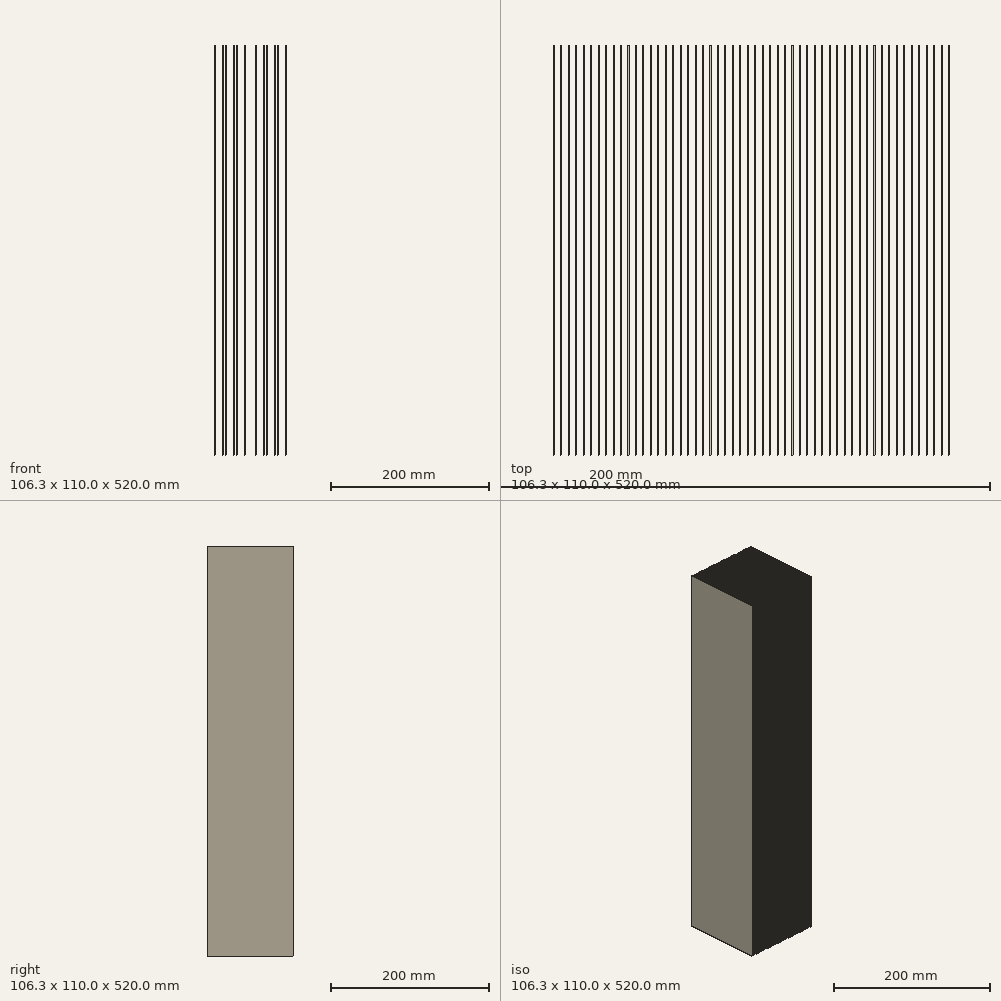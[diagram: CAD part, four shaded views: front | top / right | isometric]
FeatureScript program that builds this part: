
annotation { "Feature Type Name" : "Feature", "Feature Type Description" : "" }
export const myFeature = defineFeature(function(context is Context, id is Id, definition is map)
    precondition{}
    {
        {
            var Q0;
            Q0=qCreatedBy(makeId("Top.planeOp"),FACE);
            var sketch = newSketch(context, id + "F0", { "sketchPlane" : qUnion([Q0])});
            skLineSegment(sketch, "E0.bottom", {"start": v(-88.02, 70.44) * mm, "end": v(21.98, 70.44) * mm});
            skLineSegment(sketch, "E0.top", {"start": v(-88.02, -39.56) * mm, "end": v(21.98, -39.56) * mm});
            skLineSegment(sketch, "E0.left", {"start": v(-88.02, 70.44) * mm, "end": v(-88.02, -39.56) * mm});
            skLineSegment(sketch, "E0.right", {"start": v(21.98, 70.44) * mm, "end": v(21.98, -39.56) * mm});
            skSolve(sketch);
        }
        {
            var Q0;
            Q0 = qSketchRegion(id + "F0", true);
            extrude(context, id + "F1", {"entities" : qUnion([Q0]), "depth" : 520 * mm});
        }
        {
            var Q0;
            Q0=makeQuery(id+"F1.opExtrude","SWEPT_FACE",FACE,{"disambiguationData":[OSD([sQuery(id+"F0.wireOp",EDGE,"E0.top")])]});
            var sketch = newSketch(context, id + "F2", { "sketchPlane" : qUnion([Q0])});
            skLineSegment(sketch, "E1.bottom", {"start": v(-86.02, 520) * mm, "end": v(-85.72, 520) * mm});
            skLineSegment(sketch, "E1.top", {"start": v(-86.02, 0) * mm, "end": v(-85.72, 0) * mm});
            skLineSegment(sketch, "E1.left", {"start": v(-86.02, 520) * mm, "end": v(-86.02, 0) * mm});
            skLineSegment(sketch, "E1.right", {"start": v(-85.72, 520) * mm, "end": v(-85.72, 0) * mm});
            skLineSegment(sketch, "E2.1.0.0", {"start": v(-83.72, 520) * mm, "end": v(-83.72, 0) * mm});
            skLineSegment(sketch, "E2.1.0.1", {"start": v(-84.02, 520) * mm, "end": v(-84.02, 0) * mm});
            skLineSegment(sketch, "E2.1.0.2", {"start": v(-84.02, 0) * mm, "end": v(-83.72, 0) * mm});
            skLineSegment(sketch, "E2.1.0.3", {"start": v(-84.02, 520) * mm, "end": v(-83.72, 520) * mm});
            skLineSegment(sketch, "E2.2.0.0", {"start": v(-81.72, 520) * mm, "end": v(-81.72, 0) * mm});
            skLineSegment(sketch, "E2.2.0.1", {"start": v(-82.02, 520) * mm, "end": v(-82.02, 0) * mm});
            skLineSegment(sketch, "E2.2.0.2", {"start": v(-82.02, 0) * mm, "end": v(-81.72, 0) * mm});
            skLineSegment(sketch, "E2.2.0.3", {"start": v(-82.02, 520) * mm, "end": v(-81.72, 520) * mm});
            skLineSegment(sketch, "E2.3.0.0", {"start": v(-79.72, 520) * mm, "end": v(-79.72, 0) * mm});
            skLineSegment(sketch, "E2.3.0.1", {"start": v(-80.02, 520) * mm, "end": v(-80.02, 0) * mm});
            skLineSegment(sketch, "E2.3.0.2", {"start": v(-80.02, 0) * mm, "end": v(-79.72, 0) * mm});
            skLineSegment(sketch, "E2.3.0.3", {"start": v(-80.02, 520) * mm, "end": v(-79.72, 520) * mm});
            skLineSegment(sketch, "E2.4.0.0", {"start": v(-77.72, 520) * mm, "end": v(-77.72, 0) * mm});
            skLineSegment(sketch, "E2.4.0.1", {"start": v(-78.02, 520) * mm, "end": v(-78.02, 0) * mm});
            skLineSegment(sketch, "E2.4.0.2", {"start": v(-78.02, 0) * mm, "end": v(-77.72, 0) * mm});
            skLineSegment(sketch, "E2.4.0.3", {"start": v(-78.02, 520) * mm, "end": v(-77.72, 520) * mm});
            skLineSegment(sketch, "E2.5.0.0", {"start": v(-75.72, 520) * mm, "end": v(-75.72, 0) * mm});
            skLineSegment(sketch, "E2.5.0.1", {"start": v(-76.02, 520) * mm, "end": v(-76.02, 0) * mm});
            skLineSegment(sketch, "E2.5.0.2", {"start": v(-76.02, 0) * mm, "end": v(-75.72, 0) * mm});
            skLineSegment(sketch, "E2.5.0.3", {"start": v(-76.02, 520) * mm, "end": v(-75.72, 520) * mm});
            skLineSegment(sketch, "E2.6.0.0", {"start": v(-73.72, 520) * mm, "end": v(-73.72, 0) * mm});
            skLineSegment(sketch, "E2.6.0.1", {"start": v(-74.02, 520) * mm, "end": v(-74.02, 0) * mm});
            skLineSegment(sketch, "E2.6.0.2", {"start": v(-74.02, 0) * mm, "end": v(-73.72, 0) * mm});
            skLineSegment(sketch, "E2.6.0.3", {"start": v(-74.02, 520) * mm, "end": v(-73.72, 520) * mm});
            skLineSegment(sketch, "E2.7.0.0", {"start": v(-71.72, 520) * mm, "end": v(-71.72, 0) * mm});
            skLineSegment(sketch, "E2.7.0.1", {"start": v(-72.02, 520) * mm, "end": v(-72.02, 0) * mm});
            skLineSegment(sketch, "E2.7.0.2", {"start": v(-72.02, 0) * mm, "end": v(-71.72, 0) * mm});
            skLineSegment(sketch, "E2.7.0.3", {"start": v(-72.02, 520) * mm, "end": v(-71.72, 520) * mm});
            skLineSegment(sketch, "E2.8.0.0", {"start": v(-69.72, 520) * mm, "end": v(-69.72, 0) * mm});
            skLineSegment(sketch, "E2.8.0.1", {"start": v(-70.02, 520) * mm, "end": v(-70.02, 0) * mm});
            skLineSegment(sketch, "E2.8.0.2", {"start": v(-70.02, 0) * mm, "end": v(-69.72, 0) * mm});
            skLineSegment(sketch, "E2.8.0.3", {"start": v(-70.02, 520) * mm, "end": v(-69.72, 520) * mm});
            skLineSegment(sketch, "E2.9.0.0", {"start": v(-67.72, 520) * mm, "end": v(-67.72, 0) * mm});
            skLineSegment(sketch, "E2.9.0.1", {"start": v(-68.02, 520) * mm, "end": v(-68.02, 0) * mm});
            skLineSegment(sketch, "E2.9.0.2", {"start": v(-68.02, 0) * mm, "end": v(-67.72, 0) * mm});
            skLineSegment(sketch, "E2.9.0.3", {"start": v(-68.02, 520) * mm, "end": v(-67.72, 520) * mm});
            skLineSegment(sketch, "E2.10.0.0", {"start": v(-65.72, 520) * mm, "end": v(-65.72, 0) * mm});
            skLineSegment(sketch, "E2.10.0.1", {"start": v(-66.02, 520) * mm, "end": v(-66.02, 0) * mm});
            skLineSegment(sketch, "E2.10.0.2", {"start": v(-66.02, 0) * mm, "end": v(-65.72, 0) * mm});
            skLineSegment(sketch, "E2.10.0.3", {"start": v(-66.02, 520) * mm, "end": v(-65.72, 520) * mm});
            skLineSegment(sketch, "E2.11.0.0", {"start": v(-63.72, 520) * mm, "end": v(-63.72, 0) * mm});
            skLineSegment(sketch, "E2.11.0.1", {"start": v(-64.02, 520) * mm, "end": v(-64.02, 0) * mm});
            skLineSegment(sketch, "E2.11.0.2", {"start": v(-64.02, 0) * mm, "end": v(-63.72, 0) * mm});
            skLineSegment(sketch, "E2.11.0.3", {"start": v(-64.02, 520) * mm, "end": v(-63.72, 520) * mm});
            skLineSegment(sketch, "E2.12.0.0", {"start": v(-61.72, 520) * mm, "end": v(-61.72, 0) * mm});
            skLineSegment(sketch, "E2.12.0.1", {"start": v(-62.02, 520) * mm, "end": v(-62.02, 0) * mm});
            skLineSegment(sketch, "E2.12.0.2", {"start": v(-62.02, 0) * mm, "end": v(-61.72, 0) * mm});
            skLineSegment(sketch, "E2.12.0.3", {"start": v(-62.02, 520) * mm, "end": v(-61.72, 520) * mm});
            skLineSegment(sketch, "E2.13.0.0", {"start": v(-59.72, 520) * mm, "end": v(-59.72, 0) * mm});
            skLineSegment(sketch, "E2.13.0.1", {"start": v(-60.02, 520) * mm, "end": v(-60.02, 0) * mm});
            skLineSegment(sketch, "E2.13.0.2", {"start": v(-60.02, 0) * mm, "end": v(-59.72, 0) * mm});
            skLineSegment(sketch, "E2.13.0.3", {"start": v(-60.02, 520) * mm, "end": v(-59.72, 520) * mm});
            skLineSegment(sketch, "E2.14.0.0", {"start": v(-57.72, 520) * mm, "end": v(-57.72, 0) * mm});
            skLineSegment(sketch, "E2.14.0.1", {"start": v(-58.02, 520) * mm, "end": v(-58.02, 0) * mm});
            skLineSegment(sketch, "E2.14.0.2", {"start": v(-58.02, 0) * mm, "end": v(-57.72, 0) * mm});
            skLineSegment(sketch, "E2.14.0.3", {"start": v(-58.02, 520) * mm, "end": v(-57.72, 520) * mm});
            skLineSegment(sketch, "E2.15.0.0", {"start": v(-55.72, 520) * mm, "end": v(-55.72, 0) * mm});
            skLineSegment(sketch, "E2.15.0.1", {"start": v(-56.02, 520) * mm, "end": v(-56.02, 0) * mm});
            skLineSegment(sketch, "E2.15.0.2", {"start": v(-56.02, 0) * mm, "end": v(-55.72, 0) * mm});
            skLineSegment(sketch, "E2.15.0.3", {"start": v(-56.02, 520) * mm, "end": v(-55.72, 520) * mm});
            skLineSegment(sketch, "E2.16.0.0", {"start": v(-53.72, 520) * mm, "end": v(-53.72, 0) * mm});
            skLineSegment(sketch, "E2.16.0.1", {"start": v(-54.02, 520) * mm, "end": v(-54.02, 0) * mm});
            skLineSegment(sketch, "E2.16.0.2", {"start": v(-54.02, 0) * mm, "end": v(-53.72, 0) * mm});
            skLineSegment(sketch, "E2.16.0.3", {"start": v(-54.02, 520) * mm, "end": v(-53.72, 520) * mm});
            skLineSegment(sketch, "E2.17.0.0", {"start": v(-51.72, 520) * mm, "end": v(-51.72, 0) * mm});
            skLineSegment(sketch, "E2.17.0.1", {"start": v(-52.02, 520) * mm, "end": v(-52.02, 0) * mm});
            skLineSegment(sketch, "E2.17.0.2", {"start": v(-52.02, 0) * mm, "end": v(-51.72, 0) * mm});
            skLineSegment(sketch, "E2.17.0.3", {"start": v(-52.02, 520) * mm, "end": v(-51.72, 520) * mm});
            skLineSegment(sketch, "E2.18.0.0", {"start": v(-49.72, 520) * mm, "end": v(-49.72, 0) * mm});
            skLineSegment(sketch, "E2.18.0.1", {"start": v(-50.02, 520) * mm, "end": v(-50.02, 0) * mm});
            skLineSegment(sketch, "E2.18.0.2", {"start": v(-50.02, 0) * mm, "end": v(-49.72, 0) * mm});
            skLineSegment(sketch, "E2.18.0.3", {"start": v(-50.02, 520) * mm, "end": v(-49.72, 520) * mm});
            skLineSegment(sketch, "E2.19.0.0", {"start": v(-47.72, 520) * mm, "end": v(-47.72, 0) * mm});
            skLineSegment(sketch, "E2.19.0.1", {"start": v(-48.02, 520) * mm, "end": v(-48.02, 0) * mm});
            skLineSegment(sketch, "E2.19.0.2", {"start": v(-48.02, 0) * mm, "end": v(-47.72, 0) * mm});
            skLineSegment(sketch, "E2.19.0.3", {"start": v(-48.02, 520) * mm, "end": v(-47.72, 520) * mm});
            skLineSegment(sketch, "E2.20.0.0", {"start": v(-45.72, 520) * mm, "end": v(-45.72, 0) * mm});
            skLineSegment(sketch, "E2.20.0.1", {"start": v(-46.02, 520) * mm, "end": v(-46.02, 0) * mm});
            skLineSegment(sketch, "E2.20.0.2", {"start": v(-46.02, 0) * mm, "end": v(-45.72, 0) * mm});
            skLineSegment(sketch, "E2.20.0.3", {"start": v(-46.02, 520) * mm, "end": v(-45.72, 520) * mm});
            skLineSegment(sketch, "E2.21.0.0", {"start": v(-43.72, 520) * mm, "end": v(-43.72, 0) * mm});
            skLineSegment(sketch, "E2.21.0.1", {"start": v(-44.02, 520) * mm, "end": v(-44.02, 0) * mm});
            skLineSegment(sketch, "E2.21.0.2", {"start": v(-44.02, 0) * mm, "end": v(-43.72, 0) * mm});
            skLineSegment(sketch, "E2.21.0.3", {"start": v(-44.02, 520) * mm, "end": v(-43.72, 520) * mm});
            skLineSegment(sketch, "E2.22.0.0", {"start": v(-41.72, 520) * mm, "end": v(-41.72, 0) * mm});
            skLineSegment(sketch, "E2.22.0.1", {"start": v(-42.02, 520) * mm, "end": v(-42.02, 0) * mm});
            skLineSegment(sketch, "E2.22.0.2", {"start": v(-42.02, 0) * mm, "end": v(-41.72, 0) * mm});
            skLineSegment(sketch, "E2.22.0.3", {"start": v(-42.02, 520) * mm, "end": v(-41.72, 520) * mm});
            skLineSegment(sketch, "E2.23.0.0", {"start": v(-39.72, 520) * mm, "end": v(-39.72, 0) * mm});
            skLineSegment(sketch, "E2.23.0.1", {"start": v(-40.02, 520) * mm, "end": v(-40.02, 0) * mm});
            skLineSegment(sketch, "E2.23.0.2", {"start": v(-40.02, 0) * mm, "end": v(-39.72, 0) * mm});
            skLineSegment(sketch, "E2.23.0.3", {"start": v(-40.02, 520) * mm, "end": v(-39.72, 520) * mm});
            skLineSegment(sketch, "E2.24.0.0", {"start": v(-37.72, 520) * mm, "end": v(-37.72, 0) * mm});
            skLineSegment(sketch, "E2.24.0.1", {"start": v(-38.02, 520) * mm, "end": v(-38.02, 0) * mm});
            skLineSegment(sketch, "E2.24.0.2", {"start": v(-38.02, 0) * mm, "end": v(-37.72, 0) * mm});
            skLineSegment(sketch, "E2.24.0.3", {"start": v(-38.02, 520) * mm, "end": v(-37.72, 520) * mm});
            skLineSegment(sketch, "E2.25.0.0", {"start": v(-35.72, 520) * mm, "end": v(-35.72, 0) * mm});
            skLineSegment(sketch, "E2.25.0.1", {"start": v(-36.02, 520) * mm, "end": v(-36.02, 0) * mm});
            skLineSegment(sketch, "E2.25.0.2", {"start": v(-36.02, 0) * mm, "end": v(-35.72, 0) * mm});
            skLineSegment(sketch, "E2.25.0.3", {"start": v(-36.02, 520) * mm, "end": v(-35.72, 520) * mm});
            skLineSegment(sketch, "E2.26.0.0", {"start": v(-33.72, 520) * mm, "end": v(-33.72, 0) * mm});
            skLineSegment(sketch, "E2.26.0.1", {"start": v(-34.02, 520) * mm, "end": v(-34.02, 0) * mm});
            skLineSegment(sketch, "E2.26.0.2", {"start": v(-34.02, 0) * mm, "end": v(-33.72, 0) * mm});
            skLineSegment(sketch, "E2.26.0.3", {"start": v(-34.02, 520) * mm, "end": v(-33.72, 520) * mm});
            skLineSegment(sketch, "E2.27.0.0", {"start": v(-31.72, 520) * mm, "end": v(-31.72, 0) * mm});
            skLineSegment(sketch, "E2.27.0.1", {"start": v(-32.02, 520) * mm, "end": v(-32.02, 0) * mm});
            skLineSegment(sketch, "E2.27.0.2", {"start": v(-32.02, 0) * mm, "end": v(-31.72, 0) * mm});
            skLineSegment(sketch, "E2.27.0.3", {"start": v(-32.02, 520) * mm, "end": v(-31.72, 520) * mm});
            skLineSegment(sketch, "E2.28.0.0", {"start": v(-29.72, 520) * mm, "end": v(-29.72, 0) * mm});
            skLineSegment(sketch, "E2.28.0.1", {"start": v(-30.02, 520) * mm, "end": v(-30.02, 0) * mm});
            skLineSegment(sketch, "E2.28.0.2", {"start": v(-30.02, 0) * mm, "end": v(-29.72, 0) * mm});
            skLineSegment(sketch, "E2.28.0.3", {"start": v(-30.02, 520) * mm, "end": v(-29.72, 520) * mm});
            skLineSegment(sketch, "E2.29.0.0", {"start": v(-27.72, 520) * mm, "end": v(-27.72, 0) * mm});
            skLineSegment(sketch, "E2.29.0.1", {"start": v(-28.02, 520) * mm, "end": v(-28.02, 0) * mm});
            skLineSegment(sketch, "E2.29.0.2", {"start": v(-28.02, 0) * mm, "end": v(-27.72, 0) * mm});
            skLineSegment(sketch, "E2.29.0.3", {"start": v(-28.02, 520) * mm, "end": v(-27.72, 520) * mm});
            skLineSegment(sketch, "E2.30.0.0", {"start": v(-25.72, 520) * mm, "end": v(-25.72, 0) * mm});
            skLineSegment(sketch, "E2.30.0.1", {"start": v(-26.02, 520) * mm, "end": v(-26.02, 0) * mm});
            skLineSegment(sketch, "E2.30.0.2", {"start": v(-26.02, 0) * mm, "end": v(-25.72, 0) * mm});
            skLineSegment(sketch, "E2.30.0.3", {"start": v(-26.02, 520) * mm, "end": v(-25.72, 520) * mm});
            skLineSegment(sketch, "E2.31.0.0", {"start": v(-23.72, 520) * mm, "end": v(-23.72, 0) * mm});
            skLineSegment(sketch, "E2.31.0.1", {"start": v(-24.02, 520) * mm, "end": v(-24.02, 0) * mm});
            skLineSegment(sketch, "E2.31.0.2", {"start": v(-24.02, 0) * mm, "end": v(-23.72, 0) * mm});
            skLineSegment(sketch, "E2.31.0.3", {"start": v(-24.02, 520) * mm, "end": v(-23.72, 520) * mm});
            skLineSegment(sketch, "E2.32.0.0", {"start": v(-21.72, 520) * mm, "end": v(-21.72, 0) * mm});
            skLineSegment(sketch, "E2.32.0.1", {"start": v(-22.02, 520) * mm, "end": v(-22.02, 0) * mm});
            skLineSegment(sketch, "E2.32.0.2", {"start": v(-22.02, 0) * mm, "end": v(-21.72, 0) * mm});
            skLineSegment(sketch, "E2.32.0.3", {"start": v(-22.02, 520) * mm, "end": v(-21.72, 520) * mm});
            skLineSegment(sketch, "E2.33.0.0", {"start": v(-19.72, 520) * mm, "end": v(-19.72, 0) * mm});
            skLineSegment(sketch, "E2.33.0.1", {"start": v(-20.02, 520) * mm, "end": v(-20.02, 0) * mm});
            skLineSegment(sketch, "E2.33.0.2", {"start": v(-20.02, 0) * mm, "end": v(-19.72, 0) * mm});
            skLineSegment(sketch, "E2.33.0.3", {"start": v(-20.02, 520) * mm, "end": v(-19.72, 520) * mm});
            skLineSegment(sketch, "E2.34.0.0", {"start": v(-17.72, 520) * mm, "end": v(-17.72, 0) * mm});
            skLineSegment(sketch, "E2.34.0.1", {"start": v(-18.02, 520) * mm, "end": v(-18.02, 0) * mm});
            skLineSegment(sketch, "E2.34.0.2", {"start": v(-18.02, 0) * mm, "end": v(-17.72, 0) * mm});
            skLineSegment(sketch, "E2.34.0.3", {"start": v(-18.02, 520) * mm, "end": v(-17.72, 520) * mm});
            skLineSegment(sketch, "E2.35.0.0", {"start": v(-15.72, 520) * mm, "end": v(-15.72, 0) * mm});
            skLineSegment(sketch, "E2.35.0.1", {"start": v(-16.02, 520) * mm, "end": v(-16.02, 0) * mm});
            skLineSegment(sketch, "E2.35.0.2", {"start": v(-16.02, 0) * mm, "end": v(-15.72, 0) * mm});
            skLineSegment(sketch, "E2.35.0.3", {"start": v(-16.02, 520) * mm, "end": v(-15.72, 520) * mm});
            skLineSegment(sketch, "E2.36.0.0", {"start": v(-13.72, 520) * mm, "end": v(-13.72, 0) * mm});
            skLineSegment(sketch, "E2.36.0.1", {"start": v(-14.02, 520) * mm, "end": v(-14.02, 0) * mm});
            skLineSegment(sketch, "E2.36.0.2", {"start": v(-14.02, 0) * mm, "end": v(-13.72, 0) * mm});
            skLineSegment(sketch, "E2.36.0.3", {"start": v(-14.02, 520) * mm, "end": v(-13.72, 520) * mm});
            skLineSegment(sketch, "E2.37.0.0", {"start": v(-11.72, 520) * mm, "end": v(-11.72, 0) * mm});
            skLineSegment(sketch, "E2.37.0.1", {"start": v(-12.02, 520) * mm, "end": v(-12.02, 0) * mm});
            skLineSegment(sketch, "E2.37.0.2", {"start": v(-12.02, 0) * mm, "end": v(-11.72, 0) * mm});
            skLineSegment(sketch, "E2.37.0.3", {"start": v(-12.02, 520) * mm, "end": v(-11.72, 520) * mm});
            skLineSegment(sketch, "E2.38.0.0", {"start": v(-9.72, 520) * mm, "end": v(-9.72, 0) * mm});
            skLineSegment(sketch, "E2.38.0.1", {"start": v(-10.02, 520) * mm, "end": v(-10.02, 0) * mm});
            skLineSegment(sketch, "E2.38.0.2", {"start": v(-10.02, 0) * mm, "end": v(-9.72, 0) * mm});
            skLineSegment(sketch, "E2.38.0.3", {"start": v(-10.02, 520) * mm, "end": v(-9.72, 520) * mm});
            skLineSegment(sketch, "E2.39.0.0", {"start": v(-7.72, 520) * mm, "end": v(-7.72, 0) * mm});
            skLineSegment(sketch, "E2.39.0.1", {"start": v(-8.02, 520) * mm, "end": v(-8.02, 0) * mm});
            skLineSegment(sketch, "E2.39.0.2", {"start": v(-8.02, 0) * mm, "end": v(-7.72, 0) * mm});
            skLineSegment(sketch, "E2.39.0.3", {"start": v(-8.02, 520) * mm, "end": v(-7.72, 520) * mm});
            skLineSegment(sketch, "E2.40.0.0", {"start": v(-5.72, 520) * mm, "end": v(-5.72, 0) * mm});
            skLineSegment(sketch, "E2.40.0.1", {"start": v(-6.02, 520) * mm, "end": v(-6.02, 0) * mm});
            skLineSegment(sketch, "E2.40.0.2", {"start": v(-6.02, 0) * mm, "end": v(-5.72, 0) * mm});
            skLineSegment(sketch, "E2.40.0.3", {"start": v(-6.02, 520) * mm, "end": v(-5.72, 520) * mm});
            skLineSegment(sketch, "E2.41.0.0", {"start": v(-3.72, 520) * mm, "end": v(-3.72, 0) * mm});
            skLineSegment(sketch, "E2.41.0.1", {"start": v(-4.02, 520) * mm, "end": v(-4.02, 0) * mm});
            skLineSegment(sketch, "E2.41.0.2", {"start": v(-4.02, 0) * mm, "end": v(-3.72, 0) * mm});
            skLineSegment(sketch, "E2.41.0.3", {"start": v(-4.02, 520) * mm, "end": v(-3.72, 520) * mm});
            skLineSegment(sketch, "E2.42.0.0", {"start": v(-1.72, 520) * mm, "end": v(-1.72, 0) * mm});
            skLineSegment(sketch, "E2.42.0.1", {"start": v(-2.02, 520) * mm, "end": v(-2.02, 0) * mm});
            skLineSegment(sketch, "E2.42.0.2", {"start": v(-2.02, 0) * mm, "end": v(-1.72, 0) * mm});
            skLineSegment(sketch, "E2.42.0.3", {"start": v(-2.02, 520) * mm, "end": v(-1.72, 520) * mm});
            skLineSegment(sketch, "E2.43.0.0", {"start": v(0.28, 520) * mm, "end": v(0.28, 0) * mm});
            skLineSegment(sketch, "E2.43.0.1", {"start": v(-0.02, 520) * mm, "end": v(-0.02, 0) * mm});
            skLineSegment(sketch, "E2.43.0.2", {"start": v(-0.02, 0) * mm, "end": v(0.28, 0) * mm});
            skLineSegment(sketch, "E2.43.0.3", {"start": v(-0.02, 520) * mm, "end": v(0.28, 520) * mm});
            skLineSegment(sketch, "E2.44.0.0", {"start": v(2.28, 520) * mm, "end": v(2.28, 0) * mm});
            skLineSegment(sketch, "E2.44.0.1", {"start": v(1.98, 520) * mm, "end": v(1.98, 0) * mm});
            skLineSegment(sketch, "E2.44.0.2", {"start": v(1.98, 0) * mm, "end": v(2.28, 0) * mm});
            skLineSegment(sketch, "E2.44.0.3", {"start": v(1.98, 520) * mm, "end": v(2.28, 520) * mm});
            skLineSegment(sketch, "E2.45.0.0", {"start": v(4.28, 520) * mm, "end": v(4.28, 0) * mm});
            skLineSegment(sketch, "E2.45.0.1", {"start": v(3.98, 520) * mm, "end": v(3.98, 0) * mm});
            skLineSegment(sketch, "E2.45.0.2", {"start": v(3.98, 0) * mm, "end": v(4.28, 0) * mm});
            skLineSegment(sketch, "E2.45.0.3", {"start": v(3.98, 520) * mm, "end": v(4.28, 520) * mm});
            skLineSegment(sketch, "E2.46.0.0", {"start": v(6.28, 520) * mm, "end": v(6.28, 0) * mm});
            skLineSegment(sketch, "E2.46.0.1", {"start": v(5.98, 520) * mm, "end": v(5.98, 0) * mm});
            skLineSegment(sketch, "E2.46.0.2", {"start": v(5.98, 0) * mm, "end": v(6.28, 0) * mm});
            skLineSegment(sketch, "E2.46.0.3", {"start": v(5.98, 520) * mm, "end": v(6.28, 520) * mm});
            skLineSegment(sketch, "E2.47.0.0", {"start": v(8.28, 520) * mm, "end": v(8.28, 0) * mm});
            skLineSegment(sketch, "E2.47.0.1", {"start": v(7.98, 520) * mm, "end": v(7.98, 0) * mm});
            skLineSegment(sketch, "E2.47.0.2", {"start": v(7.98, 0) * mm, "end": v(8.28, 0) * mm});
            skLineSegment(sketch, "E2.47.0.3", {"start": v(7.98, 520) * mm, "end": v(8.28, 520) * mm});
            skLineSegment(sketch, "E2.48.0.0", {"start": v(10.28, 520) * mm, "end": v(10.28, 0) * mm});
            skLineSegment(sketch, "E2.48.0.1", {"start": v(9.98, 520) * mm, "end": v(9.98, 0) * mm});
            skLineSegment(sketch, "E2.48.0.2", {"start": v(9.98, 0) * mm, "end": v(10.28, 0) * mm});
            skLineSegment(sketch, "E2.48.0.3", {"start": v(9.98, 520) * mm, "end": v(10.28, 520) * mm});
            skLineSegment(sketch, "E2.49.0.0", {"start": v(12.28, 520) * mm, "end": v(12.28, 0) * mm});
            skLineSegment(sketch, "E2.49.0.1", {"start": v(11.98, 520) * mm, "end": v(11.98, 0) * mm});
            skLineSegment(sketch, "E2.49.0.2", {"start": v(11.98, 0) * mm, "end": v(12.28, 0) * mm});
            skLineSegment(sketch, "E2.49.0.3", {"start": v(11.98, 520) * mm, "end": v(12.28, 520) * mm});
            skLineSegment(sketch, "E2.50.0.0", {"start": v(14.28, 520) * mm, "end": v(14.28, 0) * mm});
            skLineSegment(sketch, "E2.50.0.1", {"start": v(13.98, 520) * mm, "end": v(13.98, 0) * mm});
            skLineSegment(sketch, "E2.50.0.2", {"start": v(13.98, 0) * mm, "end": v(14.28, 0) * mm});
            skLineSegment(sketch, "E2.50.0.3", {"start": v(13.98, 520) * mm, "end": v(14.28, 520) * mm});
            skLineSegment(sketch, "E2.51.0.0", {"start": v(16.28, 520) * mm, "end": v(16.28, 0) * mm});
            skLineSegment(sketch, "E2.51.0.1", {"start": v(15.98, 520) * mm, "end": v(15.98, 0) * mm});
            skLineSegment(sketch, "E2.51.0.2", {"start": v(15.98, 0) * mm, "end": v(16.28, 0) * mm});
            skLineSegment(sketch, "E2.51.0.3", {"start": v(15.98, 520) * mm, "end": v(16.28, 520) * mm});
            skLineSegment(sketch, "E2.52.0.0", {"start": v(18.28, 520) * mm, "end": v(18.28, 0) * mm});
            skLineSegment(sketch, "E2.52.0.1", {"start": v(17.98, 520) * mm, "end": v(17.98, 0) * mm});
            skLineSegment(sketch, "E2.52.0.2", {"start": v(17.98, 0) * mm, "end": v(18.28, 0) * mm});
            skLineSegment(sketch, "E2.52.0.3", {"start": v(17.98, 520) * mm, "end": v(18.28, 520) * mm});
            skLineSegment(sketch, "E2.53.0.0", {"start": v(20.28, 520) * mm, "end": v(20.28, 0) * mm});
            skLineSegment(sketch, "E2.53.0.1", {"start": v(19.98, 520) * mm, "end": v(19.98, 0) * mm});
            skLineSegment(sketch, "E2.53.0.2", {"start": v(19.98, 0) * mm, "end": v(20.28, 0) * mm});
            skLineSegment(sketch, "E2.53.0.3", {"start": v(19.98, 520) * mm, "end": v(20.28, 520) * mm});
            skLineSegment(sketch, "E2.direction1", {"start": v(-86.02, 0) * mm, "end": v(-84.02, 0) * mm, "construction": true});
            skSolve(sketch);
        }
        {
            var Q0;
            Q0 = qSketchRegion(id + "F2", true);
            extrude(context, id + "F3", {"entities" : qUnion([Q0]), "operationType" : NewBodyOperationType.ADD, "depth" : 110 * mm});
        }
        {
            var Q0;
            Q0=makeQuery(id+"F1.opExtrude","SWEPT_FACE",FACE,{"disambiguationData":[OSD([sQuery(id+"F0.wireOp",EDGE,"E0.bottom")])]});
            extrude(context, id + "F4", {"entities" : qUnion([Q0]), "operationType" : NewBodyOperationType.REMOVE, "oppositeDirection" : true, "depth" : 110 * mm});
        }
    });
